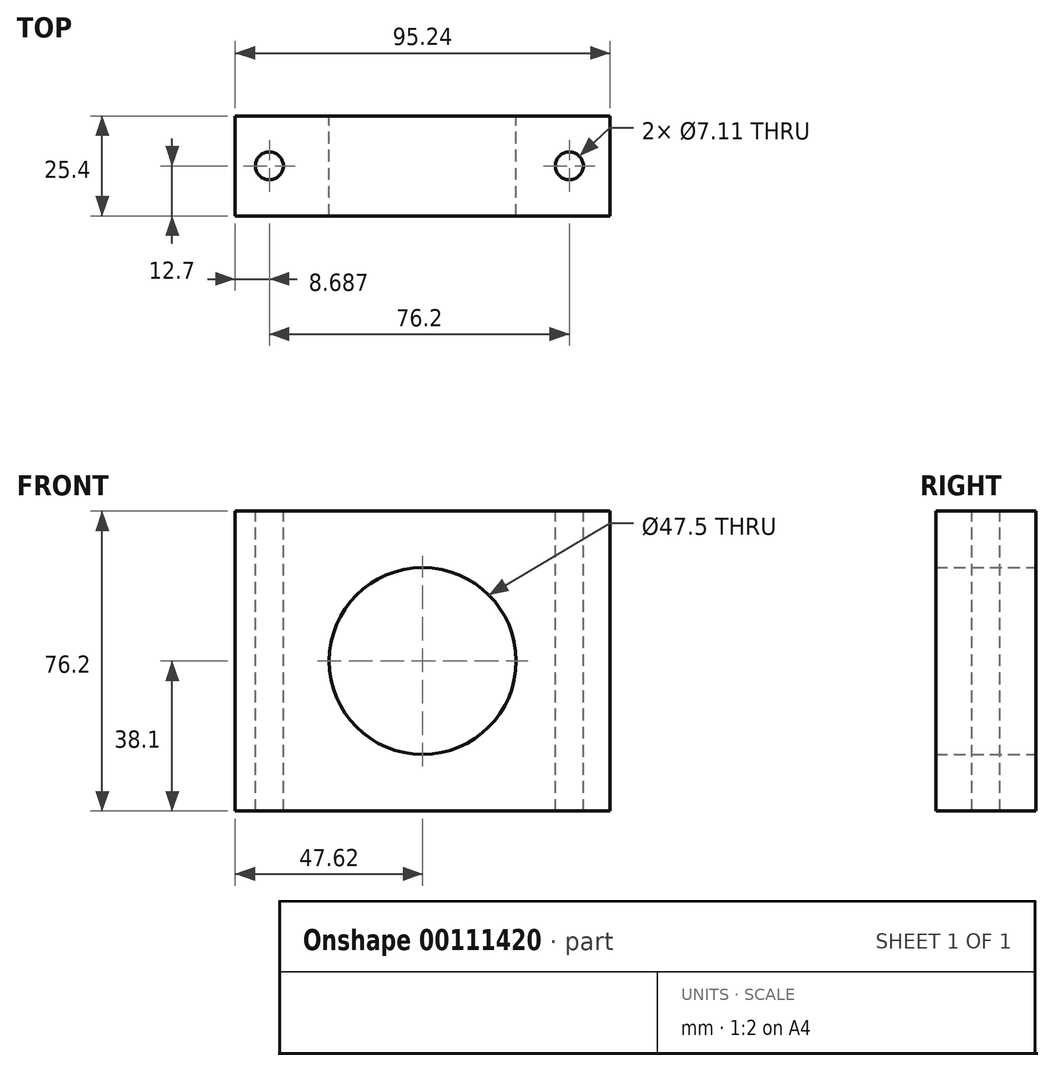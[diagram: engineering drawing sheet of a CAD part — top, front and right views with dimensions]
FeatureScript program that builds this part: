
annotation { "Feature Type Name" : "Feature", "Feature Type Description" : "" }
export const myFeature = defineFeature(function(context is Context, id is Id, definition is map)
    precondition{}
    {
        {
            var Q0;
            Q0=qCreatedBy(makeId("Front.planeOp"),FACE);
            var sketch = newSketch(context, id + "F0", { "sketchPlane" : qUnion([Q0])});
            skLineSegment(sketch, "E0.bottom", {"start": v(-47.63, 38.1) * mm, "end": v(47.62, 38.1) * mm});
            skLineSegment(sketch, "E0.top", {"start": v(-47.62, -38.1) * mm, "end": v(47.63, -38.1) * mm});
            skLineSegment(sketch, "E0.left", {"start": v(-47.62, 38.1) * mm, "end": v(-47.63, -38.1) * mm});
            skLineSegment(sketch, "E0.right", {"start": v(47.63, 38.1) * mm, "end": v(47.63, -38.1) * mm});
            skCircle(sketch, "E1", {"center": v(0, 0) * mm, "radius": 23.75 * mm});
            skPoint(sketch, "E1.centerSnap0", {"position": v(0, -38.1) * mm});
            skLineSegment(sketch, "E2", {"start": v(0, 0) * mm, "end": v(0, -38.1) * mm, "construction": true});
            skSolve(sketch);
        }
        {
            var Q0;
            Q0=qCreatedBy(makeId("Right.planeOp"),FACE);
            var sketch = newSketch(context, id + "F1", { "sketchPlane" : qUnion([Q0])});
            skSolve(sketch);
        }
        {
            var Q0;
            Q0 = qSketchRegion(id + "F1", true);
            var Q1;
            Q1=makeQuery(id+"F0.imprint","IMPRINT",FACE,{"disambiguationData":[TD([[makeQuery(id+"F0.imprint","IMPRINT",EDGE,{"derivedFrom":sQuery(id+"F0.wireOp",EDGE,"E0.bottom")}),-1.0]])]});
            extrude(context, id + "F2", {"entities" : qUnion([Q0, Q1]), "depth" : 25.4 * mm});
        }
        {
            var Q0;
            Q0=makeQuery(id+"F2.opExtrude","SWEPT_FACE",FACE,{"disambiguationData":[OSD([sQuery(id+"F0.wireOp",EDGE,"E0.bottom")])]});
            var sketch = newSketch(context, id + "F3", { "sketchPlane" : qUnion([Q0])});
            skCircle(sketch, "E3", {"center": v(-38.93, -12.7) * mm, "radius": 3.56 * mm});
            skCircle(sketch, "E4", {"center": v(37.27, -12.7) * mm, "radius": 3.56 * mm});
            skSolve(sketch);
        }
        {
            var Q0;
            Q0=makeQuery(id+"F3.imprint","IMPRINT",FACE,{"disambiguationData":[TD([[makeQuery(id+"F3.imprint","IMPRINT",EDGE,{"derivedFrom":sQuery(id+"F3.wireOp",EDGE,"E3")}),1.0]])]});
            var Q1;
            Q1=makeQuery(id+"F3.imprint","IMPRINT",FACE,{"disambiguationData":[TD([[makeQuery(id+"F3.imprint","IMPRINT",EDGE,{"derivedFrom":sQuery(id+"F3.wireOp",EDGE,"E4")}),1.0]])]});
            extrude(context, id + "F4", {"entities" : qUnion([Q0, Q1]), "operationType" : NewBodyOperationType.REMOVE, "endBound" : BoundingType.THROUGH_ALL, "oppositeDirection" : true, "depth" : 7.11 * mm});
        }
    });
